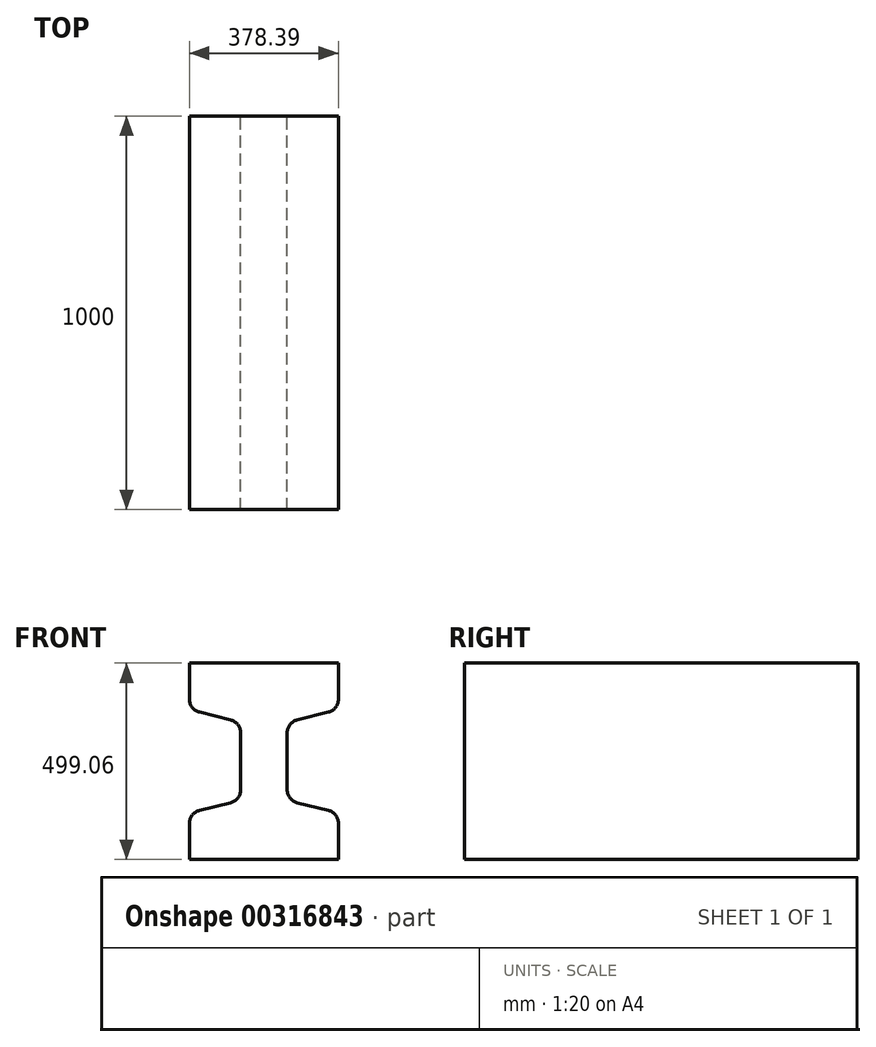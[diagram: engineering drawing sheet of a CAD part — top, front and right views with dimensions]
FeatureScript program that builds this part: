
annotation { "Feature Type Name" : "Feature", "Feature Type Description" : "" }
export const myFeature = defineFeature(function(context is Context, id is Id, definition is map)
    precondition{}
    {
        {
            var Q0;
            Q0=qCreatedBy(makeId("Front.planeOp"),FACE);
            var sketch = newSketch(context, id + "F0", { "sketchPlane" : qUnion([Q0])});
            skLineSegment(sketch, "E0", {"start": v(-11.84, 98.82) * mm, "end": v(-11.84, -98.82) * mm});
            skLineSegment(sketch, "E1", {"start": v(106.55, -98.82) * mm, "end": v(106.55, 98.82) * mm});
            skLineSegment(sketch, "E2", {"start": v(-141.84, 249.53) * mm, "end": v(-141.84, 131.14) * mm});
            skLineSegment(sketch, "E3", {"start": v(236.55, 131.14) * mm, "end": v(236.55, 249.53) * mm});
            skLineSegment(sketch, "E4", {"start": v(-141.84, 249.53) * mm, "end": v(236.55, 249.53) * mm});
            skLineSegment(sketch, "E5.MirrorCS", {"start": v(236.55, -131.14) * mm, "end": v(236.55, -249.53) * mm});
            skLineSegment(sketch, "E6.MirrorCS", {"start": v(-141.84, -249.53) * mm, "end": v(-141.84, -131.14) * mm});
            skLineSegment(sketch, "E7.MirrorCS", {"start": v(-141.84, -249.53) * mm, "end": v(236.55, -249.53) * mm});
            skLineSegment(sketch, "E8.MirrorCS", {"start": v(106.55, 98.82) * mm, "end": v(106.55, -98.82) * mm});
            skLineSegment(sketch, "E9", {"start": v(236.55, -131.14) * mm, "end": v(106.55, -98.82) * mm});
            skLineSegment(sketch, "E10.MirrorCS", {"start": v(236.55, 131.14) * mm, "end": v(106.55, 98.82) * mm});
            skLineSegment(sketch, "E11", {"start": v(47.35, 249.53) * mm, "end": v(47.35, -249.53) * mm, "construction": true});
            skLineSegment(sketch, "E12.MirrorCS", {"start": v(-141.84, 131.14) * mm, "end": v(-11.84, 98.82) * mm});
            skLineSegment(sketch, "E13.MirrorCS", {"start": v(-141.84, -131.14) * mm, "end": v(-11.84, -98.82) * mm});
            skLineSegment(sketch, "E14.trimOffspring", {"start": v(-11.84, -98.82) * mm, "end": v(-11.84, 98.82) * mm});
            skSolve(sketch);
        }
        {
            var Q0;
            Q0=makeQuery(id+"F0.imprint","IMPRINT",FACE,{"disambiguationData":[TD([[makeQuery(id+"F0.imprint","IMPRINT",EDGE,{"derivedFrom":sQuery(id+"F0.wireOp",EDGE,"E2")}),1.0]])]});
            extrude(context, id + "F1", {"entities" : qUnion([Q0]), "endBound" : BoundingType.SYMMETRIC, "depth" : 1000 * mm});
        }
        {
            var Q0;
            Q0=makeQuery(id+"F1.opExtrude","SWEPT_EDGE",EDGE,{"disambiguationData":[OSD([sQuery(id+"F0.wireOp",EDGE,"E8.MirrorCS"),sQuery(id+"F0.wireOp",EDGE,"E9")])]});
            var Q1;
            Q1=makeQuery(id+"F1.opExtrude","SWEPT_EDGE",EDGE,{"disambiguationData":[OSD([sQuery(id+"F0.wireOp",EDGE,"E12.MirrorCS"),sQuery(id+"F0.wireOp",EDGE,"E14.trimOffspring")])]});
            var Q2;
            Q2=makeQuery(id+"F1.opExtrude","SWEPT_EDGE",EDGE,{"disambiguationData":[OSD([sQuery(id+"F0.wireOp",EDGE,"E13.MirrorCS"),sQuery(id+"F0.wireOp",EDGE,"E14.trimOffspring")])]});
            var Q3;
            Q3=makeQuery(id+"F1.opExtrude","SWEPT_EDGE",EDGE,{"disambiguationData":[OSD([sQuery(id+"F0.wireOp",EDGE,"E8.MirrorCS"),sQuery(id+"F0.wireOp",EDGE,"E10.MirrorCS")])]});
            fillet(context, id + "F2", {"entities" : qUnion([Q0, Q1, Q2, Q3]), "radius" : 33.42 * mm, "tangentPropagation" : true, "allowEdgeOverflow" : false});
        }
    });
